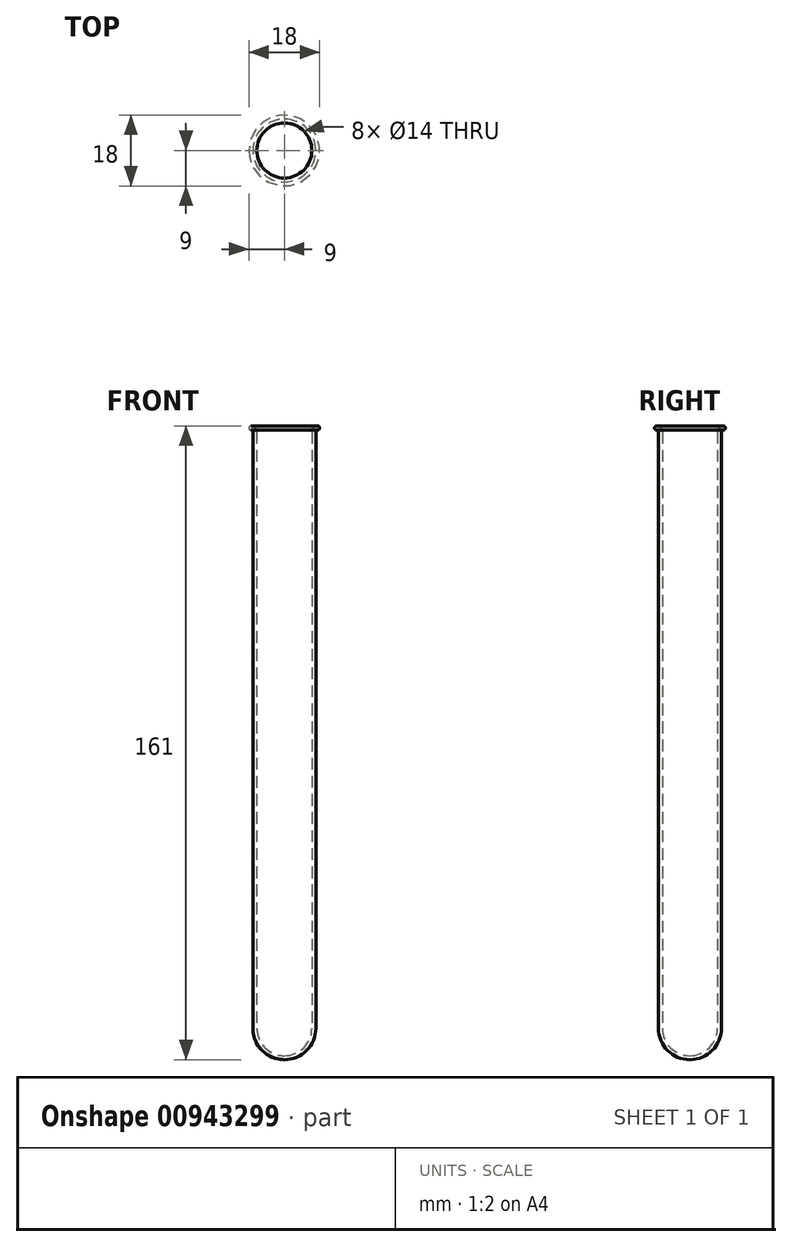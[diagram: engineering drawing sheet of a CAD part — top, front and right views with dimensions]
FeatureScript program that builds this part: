
annotation { "Feature Type Name" : "Feature", "Feature Type Description" : "" }
export const myFeature = defineFeature(function(context is Context, id is Id, definition is map)
    precondition{}
    {
        {
            var Q0;
            Q0=qCreatedBy(makeId("Front.planeOp"),FACE);
            var sketch = newSketch(context, id + "F0", { "sketchPlane" : qUnion([Q0])});
            skLineSegment(sketch, "E0", {"start": v(0, 0) * mm, "end": v(0, 168.57) * mm, "construction": true});
            skLineSegment(sketch, "E1", {"start": v(8, 159.5) * mm, "end": v(8, 8) * mm});
            skArc(sketch, "E2", {"start": v(0, 0) * mm, "mid": v(5.66, 2.34) * mm, "end": v(8, 8) * mm});
            skArc(sketch, "E3", {"start": v(8.5, 160) * mm, "mid": v(8.15, 159.85) * mm, "end": v(8, 159.5) * mm});
            skArc(sketch, "E4", {"start": v(8.5, 160) * mm, "mid": v(9, 160.5) * mm, "end": v(8.5, 161) * mm});
            skArc(sketch, "E5.0", {"start": v(0, 1) * mm, "mid": v(4.95, 3.05) * mm, "end": v(7, 8) * mm});
            skLineSegment(sketch, "E5.1", {"start": v(7, 159.5) * mm, "end": v(7, 8) * mm});
            skArc(sketch, "E5.2", {"start": v(8.5, 161) * mm, "mid": v(7.44, 160.56) * mm, "end": v(7, 159.5) * mm});
            skLineSegment(sketch, "E6", {"start": v(0, 1) * mm, "end": v(0, 0) * mm});
            skSolve(sketch);
        }
        {
            var Q0;
            Q0 = qSketchRegion(id + "F0", true);
            var Q1;
            Q1=sQuery(id+"F0.wireOp",EDGE,"E0");
            revolve(context, id + "F1", {"surfaceOperationType" : NewSurfaceOperationType.NEW, "entities" : qUnion([Q0]), "axis" : qUnion([Q1]), "revolveType" : RevolveType.FULL});
        }
    });
